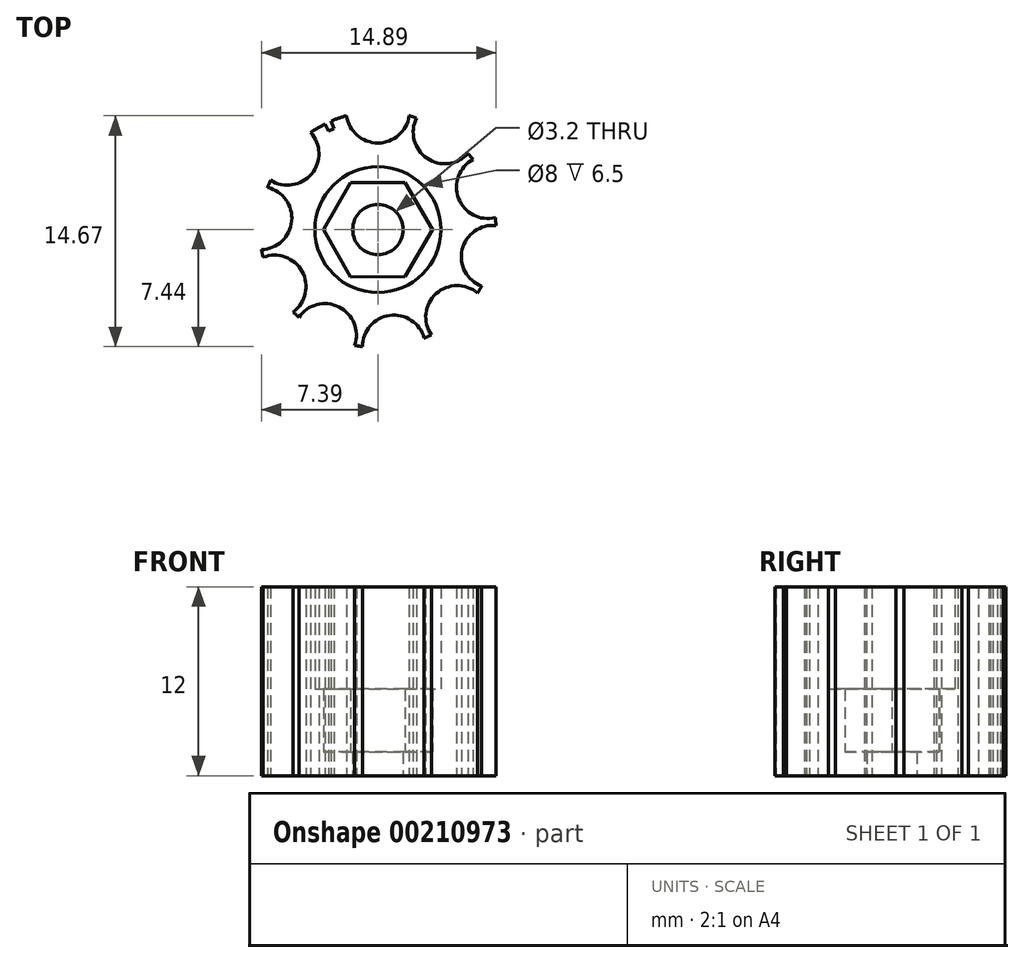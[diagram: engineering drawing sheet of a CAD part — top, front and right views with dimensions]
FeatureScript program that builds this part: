
annotation { "Feature Type Name" : "Feature", "Feature Type Description" : "" }
export const myFeature = defineFeature(function(context is Context, id is Id, definition is map)
    precondition{}
    {
        {
            var Q0;
            Q0=qCreatedBy(makeId("Top.planeOp"),FACE);
            var sketch = newSketch(context, id + "F0", { "sketchPlane" : qUnion([Q0])});
            skCircle(sketch, "E0", {"center": v(0, 0) * mm, "radius": 7.5 * mm});
            skCircle(sketch, "E1", {"center": v(0, 0) * mm, "radius": 1.6 * mm});
            skArc(sketch, "E2", {"start": v(-1.98, 7.23) * mm, "mid": v(0, 5.5) * mm, "end": v(1.98, 7.23) * mm});
            skArc(sketch, "E3.1.0", {"start": v(2.46, 7.09) * mm, "mid": v(3.11, 4.54) * mm, "end": v(5.73, 4.84) * mm});
            skArc(sketch, "E3.2.0", {"start": v(6.03, 4.45) * mm, "mid": v(5.13, 1.98) * mm, "end": v(7.46, 0.76) * mm});
            skArc(sketch, "E3.3.0", {"start": v(7.5, 0.26) * mm, "mid": v(5.35, -1.27) * mm, "end": v(6.58, -3.6) * mm});
            skArc(sketch, "E3.4.0", {"start": v(6.33, -4.02) * mm, "mid": v(3.7, -4.07) * mm, "end": v(3.4, -6.69) * mm});
            skArc(sketch, "E3.5.0", {"start": v(2.94, -6.9) * mm, "mid": v(0.74, -5.45) * mm, "end": v(-0.99, -7.44) * mm});
            skArc(sketch, "E3.6.0", {"start": v(-1.48, -7.35) * mm, "mid": v(-2.47, -4.91) * mm, "end": v(-5.02, -5.57) * mm});
            skArc(sketch, "E3.7.0", {"start": v(-5.38, -5.23) * mm, "mid": v(-4.82, -2.66) * mm, "end": v(-7.3, -1.76) * mm});
            skArc(sketch, "E3.8.0", {"start": v(-7.4, -1.27) * mm, "mid": v(-5.47, 0.53) * mm, "end": v(-7, 2.67) * mm});
            skArc(sketch, "E3.9.0", {"start": v(-6.82, 3.13) * mm, "mid": v(-4.21, 3.54) * mm, "end": v(-4.27, 6.17) * mm});
            skLineSegment(sketch, "E3.anchor1", {"start": v(0, 0) * mm, "end": v(-1.98, 7.23) * mm, "construction": true});
            skLineSegment(sketch, "E3.anchor2", {"start": v(0, 0) * mm, "end": v(-6.82, 3.13) * mm, "construction": true});
            skLineSegment(sketch, "E4", {"start": v(-3.35, 6.71) * mm, "end": v(-3.14, 6.26) * mm});
            skLineSegment(sketch, "E5.MirrorCS", {"start": v(-2.99, 6.88) * mm, "end": v(-2.78, 6.43) * mm});
            skLineSegment(sketch, "E6", {"start": v(-3.14, 6.26) * mm, "end": v(-2.78, 6.43) * mm});
            skLineSegment(sketch, "E7", {"start": v(-4.27, 6.17) * mm, "end": v(-1.98, 7.23) * mm, "construction": true});
            skLineSegment(sketch, "E8", {"start": v(-3.12, 6.7) * mm, "end": v(-2.79, 5.98) * mm, "construction": true});
            skSolve(sketch);
        }
        {
            var Q0;
            Q0=makeQuery(id+"F0.imprint","IMPRINT",FACE,{"disambiguationData":[TD([[makeQuery(id+"F0.imprint","IMPRINT",EDGE,{"derivedFrom":sQuery(id+"F0.wireOp",EDGE,"E1")}),-1.0]])]});
            extrude(context, id + "F1", {"entities" : qUnion([Q0]), "depth" : 12 * mm});
        }
        {
            var Q0;
            Q0=makeQuery(id+"F1.opExtrude","CAP_FACE",FACE,{"disambiguationData":[OSD([sQuery(id+"F0.wireOp",EDGE,"E0"),sQuery(id+"F0.wireOp",EDGE,"E1"),sQuery(id+"F0.wireOp",EDGE,"E2"),sQuery(id+"F0.wireOp",EDGE,"E3.1.0"),sQuery(id+"F0.wireOp",EDGE,"E3.2.0"),sQuery(id+"F0.wireOp",EDGE,"E3.3.0"),sQuery(id+"F0.wireOp",EDGE,"E3.4.0"),sQuery(id+"F0.wireOp",EDGE,"E3.5.0"),sQuery(id+"F0.wireOp",EDGE,"E3.6.0"),sQuery(id+"F0.wireOp",EDGE,"E3.7.0"),sQuery(id+"F0.wireOp",EDGE,"E3.8.0"),sQuery(id+"F0.wireOp",EDGE,"E3.9.0")])],"isStart":true});
            cPlane(context, id + "F2", {"entities" : qUnion([Q0]), "cplaneType" : CPlaneType.OFFSET, "offset" : 1.5 * mm, "oppositeDirection" : true, "width" : 150 * mm, "height" : 150 * mm});
        }
        {
            var Q0;
            Q0=qCreatedBy(id+"F2.planeOp",FACE);
            cPlane(context, id + "F3", {"entities" : qUnion([Q0]), "cplaneType" : CPlaneType.OFFSET, "offset" : 4 * mm, "oppositeDirection" : true, "width" : 150 * mm, "height" : 150 * mm});
        }
        {
            var Q0;
            Q0=qCreatedBy(id+"F2.planeOp",FACE);
            var sketch = newSketch(context, id + "F4", { "sketchPlane" : qUnion([Q0])});
            skCircle(sketch, "E9.cCircle", {"center": v(0, 0) * mm, "radius": 3 * mm, "construction": true});
            skLineSegment(sketch, "E9.0", {"start": v(1.74, 3) * mm, "end": v(3.46, 0) * mm});
            skLineSegment(sketch, "E9.1", {"start": v(3.46, 0) * mm, "end": v(1.73, -3) * mm});
            skLineSegment(sketch, "E9.2", {"start": v(1.73, -3) * mm, "end": v(-1.74, -3) * mm});
            skLineSegment(sketch, "E9.3", {"start": v(-1.74, -3) * mm, "end": v(-3.46, 0) * mm});
            skLineSegment(sketch, "E9.4", {"start": v(-3.46, 0) * mm, "end": v(-1.73, 3) * mm});
            skLineSegment(sketch, "E9.5", {"start": v(-1.73, 3) * mm, "end": v(1.74, 3) * mm});
            skPoint(sketch, "E9.0.midPoint", {"position": v(2.6, 1.5) * mm});
            skSolve(sketch);
        }
        {
            var Q0;
            Q0=qSketchRegion(id+"F4",true);
            var Q1;
            Q1=makeQuery(id+"F1.opExtrude","CAP_FACE",FACE,{"disambiguationData":[OSD([sQuery(id+"F0.wireOp",EDGE,"E0"),sQuery(id+"F0.wireOp",EDGE,"E1"),sQuery(id+"F0.wireOp",EDGE,"E2"),sQuery(id+"F0.wireOp",EDGE,"E3.1.0"),sQuery(id+"F0.wireOp",EDGE,"E3.2.0"),sQuery(id+"F0.wireOp",EDGE,"E3.3.0"),sQuery(id+"F0.wireOp",EDGE,"E3.4.0"),sQuery(id+"F0.wireOp",EDGE,"E3.5.0"),sQuery(id+"F0.wireOp",EDGE,"E3.6.0"),sQuery(id+"F0.wireOp",EDGE,"E3.7.0"),sQuery(id+"F0.wireOp",EDGE,"E3.8.0"),sQuery(id+"F0.wireOp",EDGE,"E3.9.0")])],"isStart":false});
            extrude(context, id + "F5", {"entities" : qUnion([Q0]), "operationType" : NewBodyOperationType.REMOVE, "oppositeDirection" : true, "endBoundEntityFace" : qUnion([Q1]), "depth" : 4 * mm});
        }
        {
            var Q0;
            Q0=qCreatedBy(id+"F3.planeOp",FACE);
            var sketch = newSketch(context, id + "F6", { "sketchPlane" : qUnion([Q0])});
            skCircle(sketch, "E10", {"center": v(0, 0) * mm, "radius": 4 * mm});
            skSolve(sketch);
        }
        {
            var Q0;
            Q0=qSketchRegion(id+"F6",true);
            var Q1;
            Q1=sQuery(id+"F6.wireOp",EDGE,"E10");
            extrude(context, id + "F7", {"entities" : qUnion([Q0]), "operationType" : NewBodyOperationType.REMOVE, "surfaceEntities" : qUnion([Q1]), "oppositeDirection" : true, "depth" : 25 * mm});
        }
    });
